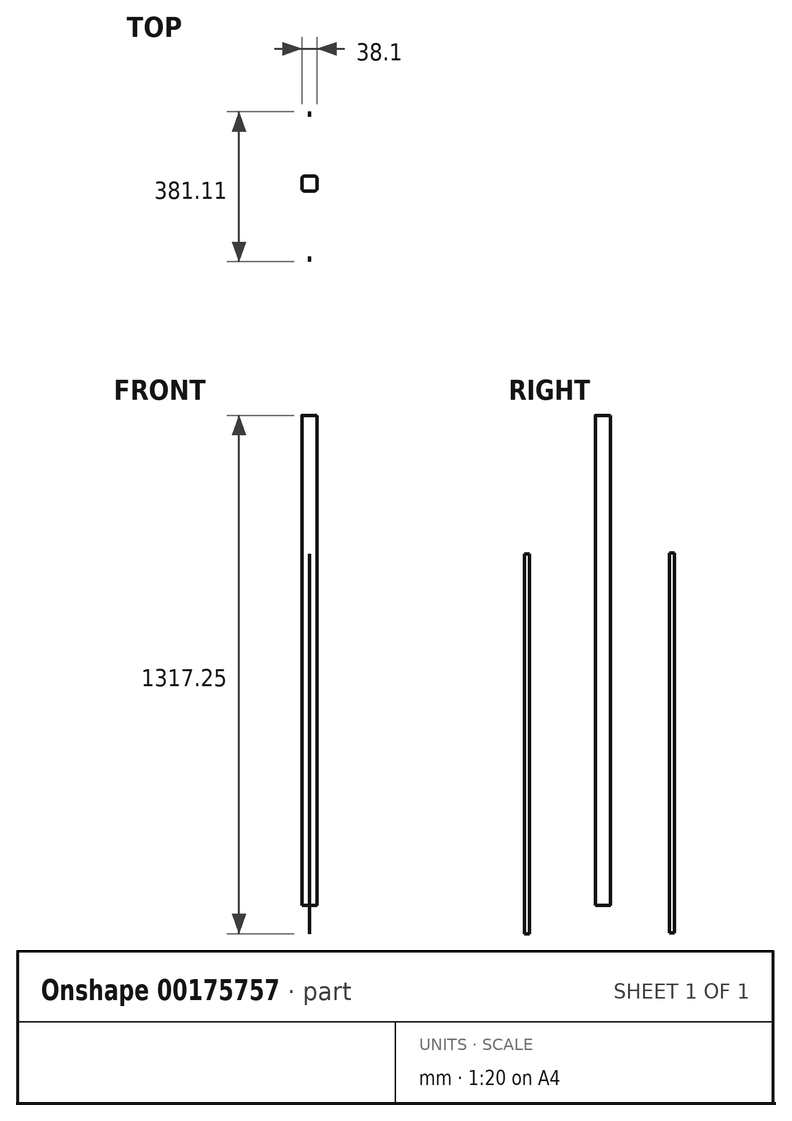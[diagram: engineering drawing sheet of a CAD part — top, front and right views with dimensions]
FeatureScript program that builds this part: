
annotation { "Feature Type Name" : "Feature", "Feature Type Description" : "" }
export const myFeature = defineFeature(function(context is Context, id is Id, definition is map)
    precondition{}
    {
        {
            var Q0;
            Q0=qCreatedBy(makeId("Top.planeOp"),FACE);
            var sketch = newSketch(context, id + "F0", { "sketchPlane" : qUnion([Q0])});
            skLineSegment(sketch, "E0.bottom", {"start": v(12.7, 19.05) * mm, "end": v(-12.7, 19.05) * mm});
            skLineSegment(sketch, "E0.top", {"start": v(12.7, -19.05) * mm, "end": v(-12.7, -19.05) * mm});
            skLineSegment(sketch, "E0.left", {"start": v(19.05, 12.7) * mm, "end": v(19.05, -12.7) * mm});
            skLineSegment(sketch, "E0.right", {"start": v(-19.05, 12.7) * mm, "end": v(-19.05, -12.7) * mm});
            skPoint(sketch, "E0.middle", {"position": v(0, 0) * mm});
            skPoint(sketch, "E1.visualSharp", {"position": v(-19.05, 19.05) * mm});
            skArc(sketch, "E1.filletArc", {"start": v(-12.7, 19.05) * mm, "mid": v(-17.2, 17.2) * mm, "end": v(-19.05, 12.7) * mm});
            skPoint(sketch, "E2.visualSharp", {"position": v(19.05, 19.05) * mm});
            skArc(sketch, "E2.filletArc", {"start": v(19.05, 12.7) * mm, "mid": v(17.2, 17.2) * mm, "end": v(12.7, 19.05) * mm});
            skPoint(sketch, "E3.visualSharp", {"position": v(19.05, -19.05) * mm});
            skArc(sketch, "E3.filletArc", {"start": v(12.7, -19.05) * mm, "mid": v(17.2, -17.2) * mm, "end": v(19.05, -12.7) * mm});
            skPoint(sketch, "E4.visualSharp", {"position": v(-19.05, -19.05) * mm});
            skArc(sketch, "E4.filletArc", {"start": v(-19.05, -12.7) * mm, "mid": v(-17.2, -17.2) * mm, "end": v(-12.7, -19.05) * mm});
            skSolve(sketch);
        }
        {
            var Q0;
            Q0=qSketchRegion(id+"F0",true);
            extrude(context, id + "F1", {"entities" : qUnion([Q0]), "depth" : 1244.6 * mm});
        }
        {
            var Q0;
            Q0=qCreatedBy(makeId("Right.planeOp"),FACE);
            var sketch = newSketch(context, id + "F2", { "sketchPlane" : qUnion([Q0])});
            skLineSegment(sketch, "E5.bottom", {"start": v(-186.2, -72.65) * mm, "end": v(-198.9, -72.65) * mm});
            skLineSegment(sketch, "E5.top", {"start": v(-186.2, 892.55) * mm, "end": v(-198.9, 892.55) * mm});
            skLineSegment(sketch, "E5.left", {"start": v(-186.2, -72.65) * mm, "end": v(-186.2, 892.55) * mm});
            skLineSegment(sketch, "E5.right", {"start": v(-198.9, -72.65) * mm, "end": v(-198.9, 892.55) * mm});
            skPoint(sketch, "E5.middle", {"position": v(-192.55, 409.95) * mm});
            skSolve(sketch);
        }
        {
            var Q0;
            Q0=qCreatedBy(makeId("Right.planeOp"),FACE);
            var sketch = newSketch(context, id + "F3", { "sketchPlane" : qUnion([Q0])});
            skLineSegment(sketch, "E6.bottom", {"start": v(182.21, -70.47) * mm, "end": v(169.51, -70.47) * mm});
            skLineSegment(sketch, "E6.top", {"start": v(182.21, 894.73) * mm, "end": v(169.51, 894.73) * mm});
            skLineSegment(sketch, "E6.left", {"start": v(182.21, -70.47) * mm, "end": v(182.21, 894.73) * mm});
            skLineSegment(sketch, "E6.right", {"start": v(169.51, -70.47) * mm, "end": v(169.51, 894.73) * mm});
            skPoint(sketch, "E6.middle", {"position": v(175.86, 412.13) * mm});
            skSolve(sketch);
        }
        {
            var Q0;
            Q0=makeQuery(id+"F2.imprint","IMPRINT",FACE,{"disambiguationData":[TD([[makeQuery(id+"F2.imprint","IMPRINT",EDGE,{"derivedFrom":sQuery(id+"F2.wireOp",EDGE,"E5.bottom")}),-1.0]])]});
            extrude(context, id + "F4", {"entities" : qUnion([Q0]), "depth" : 0.25 * mm});
        }
        {
            var Q0;
            Q0=makeQuery(id+"F3.imprint","IMPRINT",FACE,{"disambiguationData":[TD([[makeQuery(id+"F3.imprint","IMPRINT",EDGE,{"derivedFrom":sQuery(id+"F3.wireOp",EDGE,"E6.bottom")}),-1.0]])]});
            extrude(context, id + "F5", {"entities" : qUnion([Q0]), "depth" : 0.25 * mm});
        }
    });
